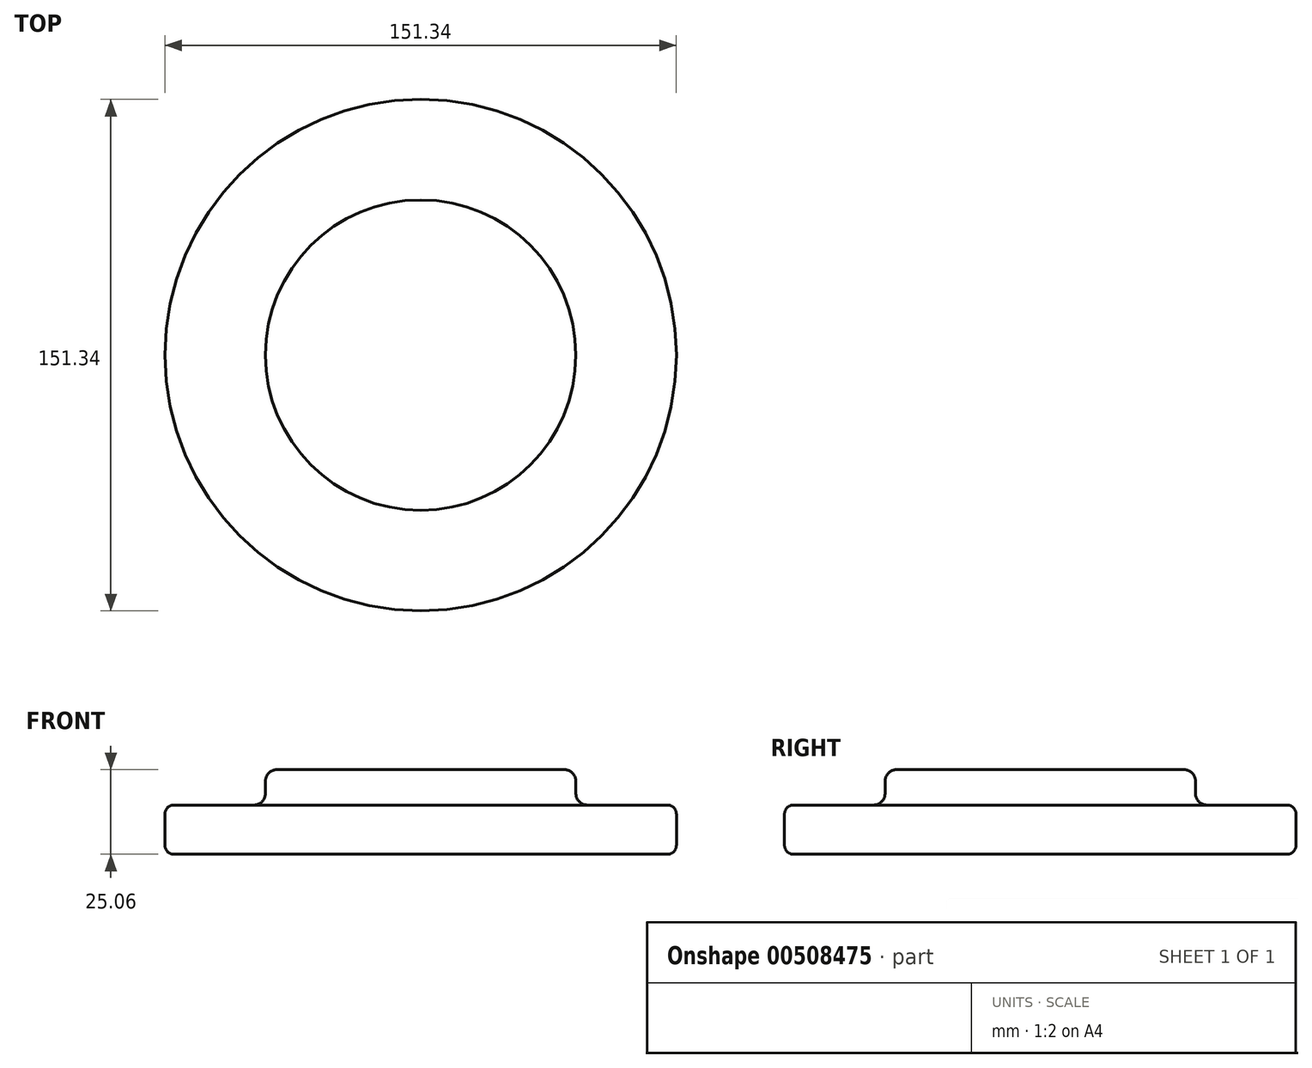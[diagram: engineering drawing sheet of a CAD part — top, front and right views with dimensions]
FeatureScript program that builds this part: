
annotation { "Feature Type Name" : "Feature", "Feature Type Description" : "" }
export const myFeature = defineFeature(function(context is Context, id is Id, definition is map)
    precondition{}
    {
        {
            var Q0;
            Q0=qCreatedBy(makeId("Top.planeOp"),FACE);
            var sketch = newSketch(context, id + "F0", { "sketchPlane" : qUnion([Q0])});
            skCircle(sketch, "E0", {"center": v(0, 0) * mm, "radius": 75.67 * mm});
            skSolve(sketch);
        }
        {
            var Q0;
            Q0=makeQuery(id+"F0.imprint","IMPRINT",FACE,{"disambiguationData":[TD([[makeQuery(id+"F0.imprint","IMPRINT",EDGE,{"derivedFrom":sQuery(id+"F0.wireOp",EDGE,"E0")}),1.0]])]});
            extrude(context, id + "F1", {"entities" : qUnion([Q0]), "depth" : 14.57 * mm});
        }
        {
            var Q0;
            Q0=makeQuery(id+"F1.opExtrude","CAP_FACE",FACE,{"disambiguationData":[OSD([sQuery(id+"F0.wireOp",EDGE,"E0")])],"isStart":false});
            var sketch = newSketch(context, id + "F2", { "sketchPlane" : qUnion([Q0])});
            skCircle(sketch, "E1", {"center": v(0, 0) * mm, "radius": 45.93 * mm});
            skSolve(sketch);
        }
        {
            var Q0;
            Q0=makeQuery(id+"F2.imprint","IMPRINT",FACE,{"disambiguationData":[TD([[makeQuery(id+"F2.imprint","IMPRINT",EDGE,{"derivedFrom":sQuery(id+"F2.wireOp",EDGE,"E1")}),1.0]])]});
            extrude(context, id + "F3", {"entities" : qUnion([Q0]), "operationType" : NewBodyOperationType.ADD, "depth" : 10.5 * mm});
        }
        {
            var Q0;
            Q0=makeQuery(id+"F3.opExtrude","SWEPT_FACE",FACE,{"disambiguationData":[OSD([sQuery(id+"F2.wireOp",EDGE,"E1")])]});
            var Q1;
            Q1=makeQuery(id+"F3.opExtrude","CAP_FACE",FACE,{"disambiguationData":[OSD([sQuery(id+"F2.wireOp",EDGE,"E1")])],"isStart":false});
            fillet(context, id + "F4", {"entities" : qUnion([Q0, Q1]), "radius" : 3.44 * mm, "tangentPropagation" : true, "allowEdgeOverflow" : false});
        }
        {
            var Q0;
            Q0=makeQuery(id+"F1.opExtrude","SWEPT_FACE",FACE,{"disambiguationData":[OSD([sQuery(id+"F0.wireOp",EDGE,"E0")])]});
            fillet(context, id + "F5", {"entities" : qUnion([Q0]), "radius" : 2.67 * mm, "tangentPropagation" : true, "allowEdgeOverflow" : false});
        }
    });
